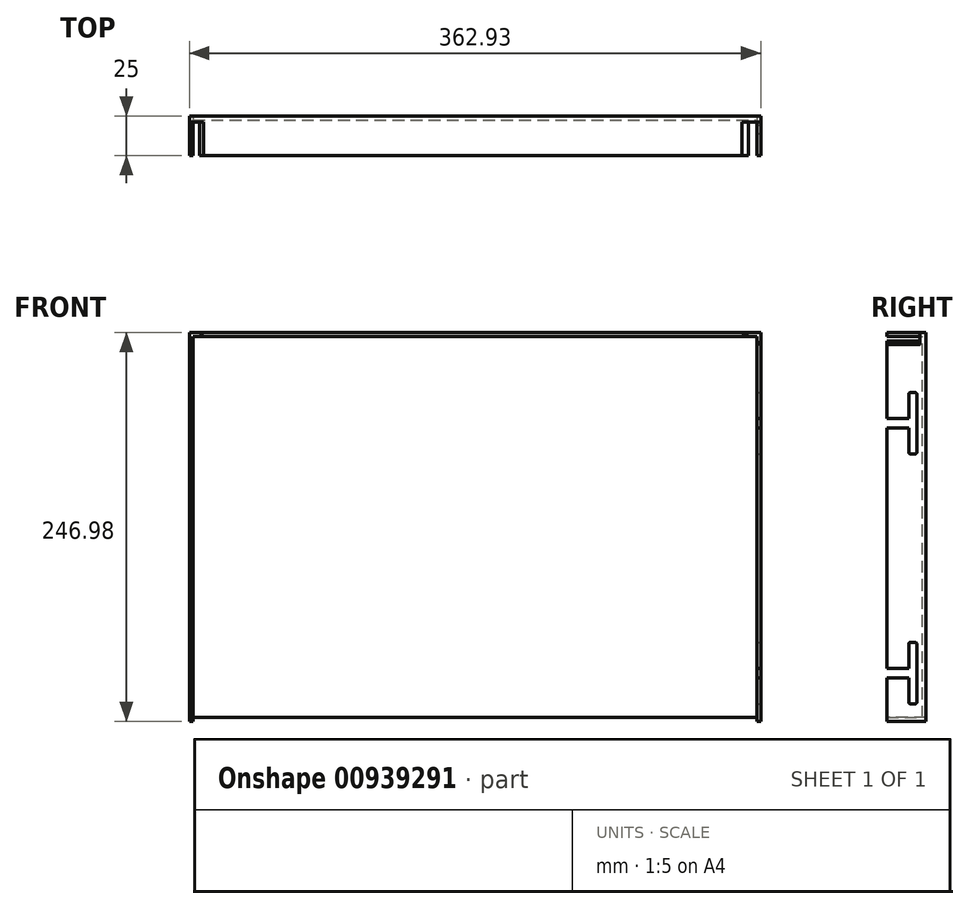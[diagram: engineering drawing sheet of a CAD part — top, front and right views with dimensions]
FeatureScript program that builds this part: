
annotation { "Feature Type Name" : "Feature", "Feature Type Description" : "" }
export const myFeature = defineFeature(function(context is Context, id is Id, definition is map)
    precondition{}
    {
        {
            var Q0;
            Q0=qCreatedBy(makeId("Front.planeOp"),FACE);
            var sketch = newSketch(context, id + "F0", { "sketchPlane" : qUnion([Q0])});
            skLineSegment(sketch, "E0.bottom", {"start": v(15.99, -160.82) * mm, "end": v(378.92, -160.82) * mm});
            skLineSegment(sketch, "E0.top", {"start": v(15.99, 86.16) * mm, "end": v(378.92, 86.16) * mm});
            skLineSegment(sketch, "E0.left", {"start": v(15.99, -160.82) * mm, "end": v(15.99, 86.16) * mm});
            skLineSegment(sketch, "E0.right", {"start": v(378.92, -160.82) * mm, "end": v(378.92, 86.16) * mm});
            skSolve(sketch);
        }
        {
            var Q0;
            Q0=makeQuery(id+"F0.imprint","IMPRINT",FACE,{"disambiguationData":[TD([[makeQuery(id+"F0.imprint","IMPRINT",EDGE,{"derivedFrom":sQuery(id+"F0.wireOp",EDGE,"E0.bottom")}),1.0]])]});
            extrude(context, id + "F1", {"entities" : qUnion([Q0]), "depth" : 25 * mm, "offsetDistance" : 25 * mm});
        }
        {
            var Q0;
            Q0=makeQuery(id+"F1.opExtrude","CAP_FACE",FACE,{"disambiguationData":[OSD([sQuery(id+"F0.wireOp",EDGE,"E0.bottom"),sQuery(id+"F0.wireOp",EDGE,"E0.top"),sQuery(id+"F0.wireOp",EDGE,"E0.left"),sQuery(id+"F0.wireOp",EDGE,"E0.right")])],"isStart":false});
            shell(context, id + "F2", {"entities" : qUnion([Q0]), "thickness" : 2.5 * mm});
        }
        {
            var Q0;
            Q0=makeQuery(id+"F1.opExtrude","CAP_FACE",FACE,{"disambiguationData":[OSD([sQuery(id+"F0.wireOp",EDGE,"E0.bottom"),sQuery(id+"F0.wireOp",EDGE,"E0.top"),sQuery(id+"F0.wireOp",EDGE,"E0.left"),sQuery(id+"F0.wireOp",EDGE,"E0.right")])],"isStart":false});
            var sketch = newSketch(context, id + "F3", { "sketchPlane" : qUnion([Q0])});
            skLineSegment(sketch, "E1.bottom", {"start": v(18.49, -158.32) * mm, "end": v(376.44, -158.32) * mm});
            skLineSegment(sketch, "E1.top", {"start": v(18.49, -203.64) * mm, "end": v(376.44, -203.64) * mm});
            skLineSegment(sketch, "E1.left", {"start": v(18.49, -158.32) * mm, "end": v(18.49, -203.64) * mm});
            skLineSegment(sketch, "E1.right", {"start": v(376.44, -158.32) * mm, "end": v(376.44, -203.64) * mm});
            skSolve(sketch);
        }
        {
            var Q0;
            Q0 = qSketchRegion(id + "F3", true);
            extrude(context, id + "F4", {"entities" : qUnion([Q0]), "operationType" : NewBodyOperationType.REMOVE, "oppositeDirection" : true, "depth" : 25 * mm, "offsetDistance" : 25 * mm});
        }
        {
            var Q0;
            Q0=makeQuery(id+"F1.opExtrude","SWEPT_FACE",FACE,{"disambiguationData":[OSD([sQuery(id+"F0.wireOp",EDGE,"E0.right")])]});
            var sketch = newSketch(context, id + "F5", { "sketchPlane" : qUnion([Q0])});
            skLineSegment(sketch, "E2.bottom", {"start": v(-29.86, 31.48) * mm, "end": v(-11.04, 31.48) * mm});
            skLineSegment(sketch, "E2.top", {"start": v(-29.86, 25.64) * mm, "end": v(-11.04, 25.64) * mm});
            skLineSegment(sketch, "E2.left", {"start": v(-29.86, 31.48) * mm, "end": v(-29.86, 25.64) * mm});
            skLineSegment(sketch, "E3.bottom", {"start": v(-10.04, 48.03) * mm, "end": v(-6.84, 48.03) * mm});
            skLineSegment(sketch, "E3.top", {"start": v(-10.04, 9.08) * mm, "end": v(-6.84, 9.08) * mm});
            skLineSegment(sketch, "E3.left", {"start": v(-11.04, 47.03) * mm, "end": v(-11.04, 31.48) * mm});
            skLineSegment(sketch, "E3.right", {"start": v(-5.84, 47.03) * mm, "end": v(-5.84, 10.08) * mm});
            skLineSegment(sketch, "E4.trimOffspring", {"start": v(-11.04, 25.64) * mm, "end": v(-11.04, 10.08) * mm});
            skPoint(sketch, "E5.visualSharp", {"position": v(-5.84, 48.03) * mm});
            skArc(sketch, "E5.filletArc", {"start": v(-5.84, 47.03) * mm, "mid": v(-6.14, 47.74) * mm, "end": v(-6.84, 48.03) * mm});
            skPoint(sketch, "E6.visualSharp", {"position": v(-11.04, 48.03) * mm});
            skArc(sketch, "E6.filletArc", {"start": v(-10.04, 48.03) * mm, "mid": v(-10.74, 47.74) * mm, "end": v(-11.04, 47.03) * mm});
            skPoint(sketch, "E7.visualSharp", {"position": v(-5.84, 9.08) * mm});
            skArc(sketch, "E7.filletArc", {"start": v(-6.84, 9.08) * mm, "mid": v(-6.14, 9.38) * mm, "end": v(-5.84, 10.08) * mm});
            skPoint(sketch, "E8.visualSharp", {"position": v(-11.04, 9.08) * mm});
            skArc(sketch, "E8.filletArc", {"start": v(-11.04, 10.08) * mm, "mid": v(-10.74, 9.38) * mm, "end": v(-10.04, 9.08) * mm});
            skLineSegment(sketch, "E9.bottom", {"start": v(-29.86, -127.23) * mm, "end": v(-11.04, -127.23) * mm});
            skLineSegment(sketch, "E9.top", {"start": v(-29.86, -133.07) * mm, "end": v(-11.04, -133.07) * mm});
            skLineSegment(sketch, "E9.left", {"start": v(-29.86, -127.23) * mm, "end": v(-29.86, -133.07) * mm});
            skLineSegment(sketch, "E10.bottom", {"start": v(-10.04, -110.67) * mm, "end": v(-6.84, -110.67) * mm});
            skLineSegment(sketch, "E10.top", {"start": v(-10.04, -149.62) * mm, "end": v(-6.84, -149.62) * mm});
            skLineSegment(sketch, "E10.left", {"start": v(-11.04, -111.67) * mm, "end": v(-11.04, -127.23) * mm});
            skLineSegment(sketch, "E10.right", {"start": v(-5.84, -111.67) * mm, "end": v(-5.84, -148.62) * mm});
            skLineSegment(sketch, "E11.trimOffspring", {"start": v(-11.04, -133.07) * mm, "end": v(-11.04, -148.62) * mm});
            skPoint(sketch, "E12.visualSharp", {"position": v(-5.84, -110.67) * mm});
            skArc(sketch, "E12.filletArc", {"start": v(-5.84, -111.67) * mm, "mid": v(-6.14, -110.97) * mm, "end": v(-6.84, -110.67) * mm});
            skPoint(sketch, "E13.visualSharp", {"position": v(-11.04, -110.67) * mm});
            skArc(sketch, "E13.filletArc", {"start": v(-10.04, -110.67) * mm, "mid": v(-10.74, -110.97) * mm, "end": v(-11.04, -111.67) * mm});
            skPoint(sketch, "E14.visualSharp", {"position": v(-5.84, -149.62) * mm});
            skArc(sketch, "E14.filletArc", {"start": v(-6.84, -149.62) * mm, "mid": v(-6.14, -149.33) * mm, "end": v(-5.84, -148.62) * mm});
            skPoint(sketch, "E15.visualSharp", {"position": v(-11.04, -149.62) * mm});
            skArc(sketch, "E15.filletArc", {"start": v(-11.04, -148.62) * mm, "mid": v(-10.74, -149.33) * mm, "end": v(-10.04, -149.62) * mm});
            skSolve(sketch);
        }
        {
            var Q0;
            Q0=makeQuery(id+"F5.imprint","IMPRINT",FACE,{"disambiguationData":[TD([[makeQuery(id+"F5.imprint","IMPRINT",EDGE,{"derivedFrom":sQuery(id+"F5.wireOp",EDGE,"E3.bottom")}),-1.0]])]});
            var Q1;
            Q1=makeQuery(id+"F5.imprint","IMPRINT",FACE,{"disambiguationData":[TD([[makeQuery(id+"F5.imprint","IMPRINT",EDGE,{"derivedFrom":sQuery(id+"F5.wireOp",EDGE,"E10.bottom")}),-1.0]])]});
            extrude(context, id + "F6", {"entities" : qUnion([Q0, Q1]), "operationType" : NewBodyOperationType.REMOVE, "oppositeDirection" : true, "depth" : 407 * mm, "offsetDistance" : 25 * mm});
        }
        {
            var Q0;
            {var subQ0=sQuery(id+"F0.wireOp",EDGE,"E0.right");var subQ1=sQuery(id+"F0.wireOp",EDGE,"E0.left");var subQ2=sQuery(id+"F0.wireOp",EDGE,"E0.top");Q0=makeQuery(id+"F6.boolean.opBoolean","SPLIT",FACE,{"disambiguationData":[TD([makeQuery(id+"F1.opExtrude","SWEPT_FACE",FACE,{"disambiguationData":[OSD([subQ2])]}),makeQuery(id+"F1.opExtrude","SWEPT_FACE",FACE,{"disambiguationData":[OSD([subQ1])]}),makeQuery(id+"F1.opExtrude","SWEPT_FACE",FACE,{"disambiguationData":[OSD([subQ0])]}),makeQuery(id+"F2.opShell","OFFSET_FACE",FACE,{"disambiguationData":[OSD([subQ2])]}),makeQuery(id+"F2.opShell","OFFSET_FACE",FACE,{"disambiguationData":[OSD([subQ1])]}),makeQuery(id+"F2.opShell","OFFSET_FACE",FACE,{"disambiguationData":[OSD([subQ0])]}),makeQuery(id+"F6.opExtrude","SWEPT_FACE",FACE,{"disambiguationData":[OSD([sQuery(id+"F5.wireOp",EDGE,"E2.bottom")])]})])],"derivedFrom":makeQuery(id+"F1.opExtrude","CAP_FACE",FACE,{"disambiguationData":[OSD([sQuery(id+"F0.wireOp",EDGE,"E0.bottom"),subQ2,subQ1,subQ0])],"isStart":false})});}
            var sketch = newSketch(context, id + "F7", { "sketchPlane" : qUnion([Q0])});
            skLineSegment(sketch, "E16", {"start": v(16.72, 77.8) * mm, "end": v(26.7, 88.02) * mm});
            skLineSegment(sketch, "E17", {"start": v(26.7, 88.02) * mm, "end": v(14.18, 88.02) * mm});
            skLineSegment(sketch, "E18", {"start": v(14.18, 88.02) * mm, "end": v(16.72, 77.8) * mm});
            skLineSegment(sketch, "E19", {"start": v(366.9, 87.58) * mm, "end": v(367.06, 86.16) * mm});
            skLineSegment(sketch, "E20", {"start": v(367.06, 86.16) * mm, "end": v(380.2, 77.8) * mm});
            skLineSegment(sketch, "E21", {"start": v(380.2, 77.8) * mm, "end": v(380.2, 91.04) * mm});
            skLineSegment(sketch, "E22", {"start": v(380.2, 91.04) * mm, "end": v(367.06, 86.16) * mm});
            skSolve(sketch);
        }
        {
            var Q0;
            {var subQ1=sQuery(id+"F0.wireOp",EDGE,"E0.top");var subQ6=makeQuery(id+"F1.opExtrude","CAP_EDGE",EDGE,{"disambiguationData":[OSD([subQ1])],"isStart":false});var subQ8=sQuery(id+"F7.wireOp",EDGE,"E20");var subQ11=makeQuery(id+"F2.opShell","OFFSET_EDGE",EDGE,{"disambiguationData":[OSD([subQ1]),TDD([subQ6])]});var subQ14=makeQuery(id+"F7.imprint","INTERSECT",VERTEX,{"derivedFrom":[subQ11,subQ8]});Q0=makeQuery(id+"F7.imprint","IMPRINT",FACE,{"disambiguationData":[TD([[makeQuery(id+"F7.imprint","IMPRINT",EDGE,{"disambiguationData":[TD([[subQ14,1.0]])],"derivedFrom":subQ8}),1.0]])]});}
            var Q1;
            {var subQ1=sQuery(id+"F7.wireOp",EDGE,"E16");var subQ4=sQuery(id+"F0.wireOp",EDGE,"E0.top");var subQ10=makeQuery(id+"F1.opExtrude","CAP_EDGE",EDGE,{"disambiguationData":[OSD([subQ4])],"isStart":false});var subQ12=makeQuery(id+"F7.imprint","INTERSECT",VERTEX,{"derivedFrom":[subQ10,subQ1]});Q1=makeQuery(id+"F7.imprint","IMPRINT",FACE,{"disambiguationData":[TD([[makeQuery(id+"F7.imprint","IMPRINT",EDGE,{"disambiguationData":[TD([[subQ12,1.0]])],"derivedFrom":subQ1}),1.0]])]});}
            extrude(context, id + "F8", {"entities" : qUnion([Q0, Q1]), "operationType" : NewBodyOperationType.REMOVE, "oppositeDirection" : true, "depth" : 21.2 * mm, "offsetDistance" : 25 * mm});
        }
    });
